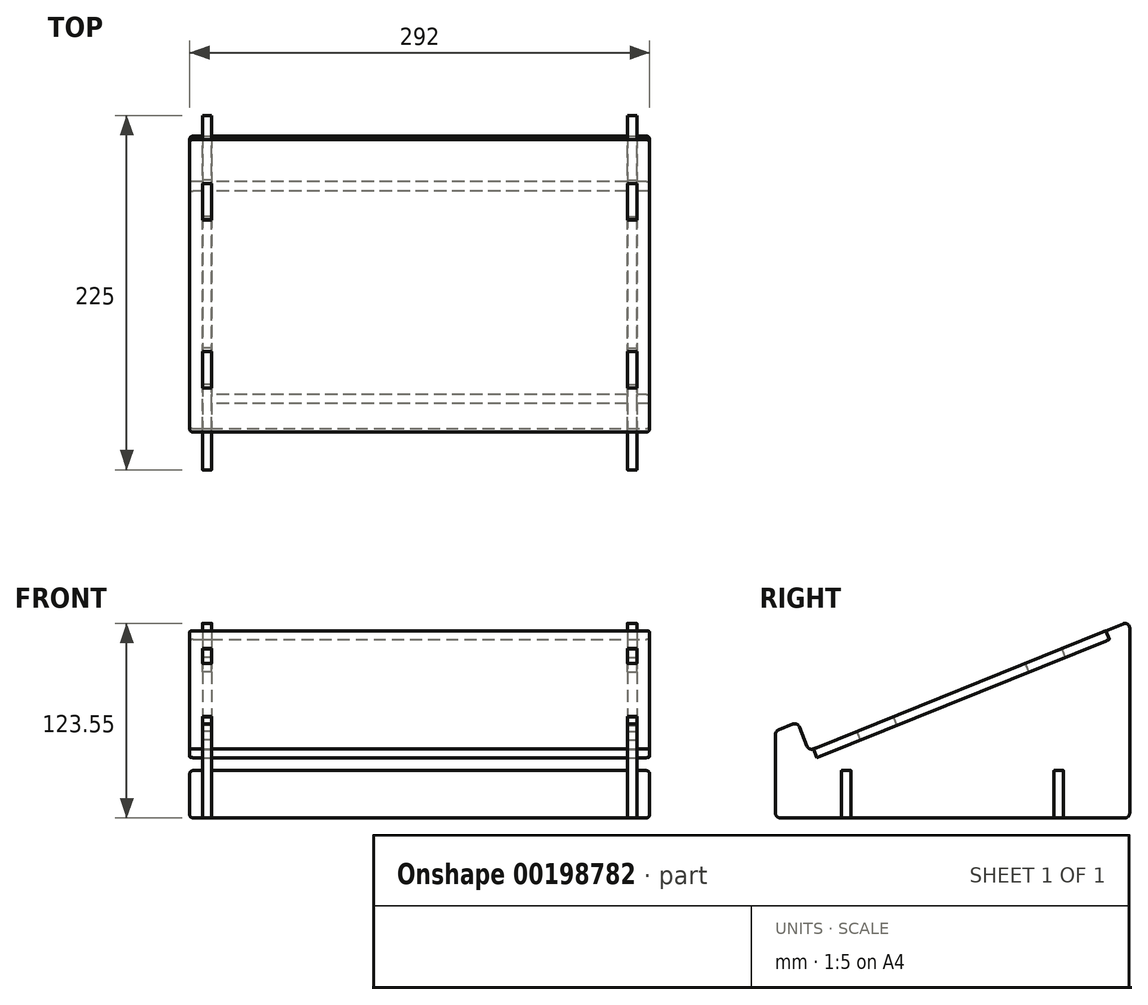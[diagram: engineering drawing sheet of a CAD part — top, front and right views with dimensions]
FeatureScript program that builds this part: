
annotation { "Feature Type Name" : "Feature", "Feature Type Description" : "" }
export const myFeature = defineFeature(function(context is Context, id is Id, definition is map)
    precondition{}
    {
        {
            var Q0;
            Q0=qCreatedBy(makeId("Right.planeOp"),FACE);
            var sketch = newSketch(context, id + "F0", { "sketchPlane" : qUnion([Q0])});
            skLineSegment(sketch, "E0", {"start": v(0, 0) * mm, "end": v(225, 0) * mm});
            skLineSegment(sketch, "E1", {"start": v(225, 0) * mm, "end": v(225, 125) * mm});
            skLineSegment(sketch, "E2", {"start": v(225, 125) * mm, "end": v(21.26, 42.68) * mm});
            skLineSegment(sketch, "E3", {"start": v(21.26, 42.68) * mm, "end": v(14, 60.66) * mm});
            skLineSegment(sketch, "E4", {"start": v(14, 60.66) * mm, "end": v(0, 55) * mm});
            skLineSegment(sketch, "E5", {"start": v(0, 55) * mm, "end": v(0, 0) * mm});
            skSolve(sketch);
        }
        {
            var Q0;
            Q0=makeQuery(id+"F0.imprint","IMPRINT",FACE,{"disambiguationData":[TD([[makeQuery(id+"F0.imprint","IMPRINT",EDGE,{"derivedFrom":sQuery(id+"F0.wireOp",EDGE,"E0")}),1.0]])]});
            extrude(context, id + "F1", {"entities" : qUnion([Q0]), "depth" : 6 * mm});
        }
        {
            var Q0;
            Q0=makeQuery(id+"F1.opExtrude","SWEPT_EDGE",EDGE,{"disambiguationData":[OSD([sQuery(id+"F0.wireOp",EDGE,"E1"),sQuery(id+"F0.wireOp",EDGE,"E2")])]});
            var Q1;
            Q1=makeQuery(id+"F1.opExtrude","SWEPT_EDGE",EDGE,{"disambiguationData":[OSD([sQuery(id+"F0.wireOp",EDGE,"E0"),sQuery(id+"F0.wireOp",EDGE,"E1")])]});
            var Q2;
            Q2=makeQuery(id+"F1.opExtrude","SWEPT_EDGE",EDGE,{"disambiguationData":[OSD([sQuery(id+"F0.wireOp",EDGE,"E4"),sQuery(id+"F0.wireOp",EDGE,"E5")])]});
            var Q3;
            Q3=makeQuery(id+"F1.opExtrude","SWEPT_EDGE",EDGE,{"disambiguationData":[OSD([sQuery(id+"F0.wireOp",EDGE,"E3"),sQuery(id+"F0.wireOp",EDGE,"E4")])]});
            var Q4;
            Q4=makeQuery(id+"F1.opExtrude","SWEPT_EDGE",EDGE,{"disambiguationData":[OSD([sQuery(id+"F0.wireOp",EDGE,"E2"),sQuery(id+"F0.wireOp",EDGE,"E3")])]});
            var Q5;
            Q5=makeQuery(id+"F1.opExtrude","SWEPT_EDGE",EDGE,{"disambiguationData":[OSD([sQuery(id+"F0.wireOp",EDGE,"E0"),sQuery(id+"F0.wireOp",EDGE,"E5")])]});
            fillet(context, id + "F2", {"entities" : qUnion([Q0, Q1, Q2, Q3, Q4, Q5]), "radius" : 3 * mm, "tangentPropagation" : true, "allowEdgeOverflow" : false});
        }
        {
            var Q0;
            Q0=makeQuery(id+"F1.opExtrude","SWEPT_BODY",BODY,{"disambiguationData":[OSD([sQuery(id+"F0.wireOp",EDGE,"E0"),sQuery(id+"F0.wireOp",EDGE,"E1"),sQuery(id+"F0.wireOp",EDGE,"E2"),sQuery(id+"F0.wireOp",EDGE,"E3"),sQuery(id+"F0.wireOp",EDGE,"E4"),sQuery(id+"F0.wireOp",EDGE,"E5")])]});
            transform(context, id + "F3", {"entities" : qUnion([Q0]), "transformType" : TransformType.TRANSLATION_3D, "dx" : 270 * mm, "dy" : 0 * mm, "dz" : 0 * mm, "makeCopy" : true});
        }
        {
            var Q0;
            Q0=makeQuery(id+"F1.opExtrude","SWEPT_FACE",FACE,{"disambiguationData":[OSD([sQuery(id+"F0.wireOp",EDGE,"E2")])]});
            var sketch = newSketch(context, id + "F4", { "sketchPlane" : qUnion([Q0])});
            skLineSegment(sketch, "E6.bottom", {"start": v(-8, 239) * mm, "end": v(284, 239) * mm});
            skLineSegment(sketch, "E6.top", {"start": v(-8, 38.7) * mm, "end": v(284, 38.7) * mm});
            skLineSegment(sketch, "E6.left", {"start": v(-8, 239) * mm, "end": v(-8, 38.7) * mm});
            skLineSegment(sketch, "E6.right", {"start": v(284, 239) * mm, "end": v(284, 38.7) * mm});
            skLineSegment(sketch, "E7.bottom", {"start": v(270, 209) * mm, "end": v(276, 209) * mm});
            skLineSegment(sketch, "E7.top", {"start": v(270, 184) * mm, "end": v(276, 184) * mm});
            skLineSegment(sketch, "E7.left", {"start": v(270, 209) * mm, "end": v(270, 184) * mm});
            skLineSegment(sketch, "E7.right", {"start": v(276, 209) * mm, "end": v(276, 184) * mm});
            skLineSegment(sketch, "E8", {"start": v(138, 239) * mm, "end": v(138, 38.7) * mm, "construction": true});
            skLineSegment(sketch, "E9", {"start": v(-8, 138.85) * mm, "end": v(284, 138.85) * mm, "construction": true});
            skLineSegment(sketch, "E10.MirrorCS", {"start": v(6, 209) * mm, "end": v(6, 184) * mm});
            skLineSegment(sketch, "E11.MirrorCS", {"start": v(6, 209) * mm, "end": v(0, 209) * mm});
            skLineSegment(sketch, "E12.MirrorCS", {"start": v(0, 209) * mm, "end": v(0, 184) * mm});
            skLineSegment(sketch, "E13.MirrorCS", {"start": v(6, 184) * mm, "end": v(0, 184) * mm});
            skLineSegment(sketch, "E14.MirrorCS", {"start": v(6, 68.7) * mm, "end": v(6, 93.7) * mm});
            skLineSegment(sketch, "E15.MirrorCS", {"start": v(6, 68.7) * mm, "end": v(0, 68.7) * mm});
            skLineSegment(sketch, "E16.MirrorCS", {"start": v(0, 68.7) * mm, "end": v(0, 93.7) * mm});
            skLineSegment(sketch, "E17.MirrorCS", {"start": v(6, 93.7) * mm, "end": v(0, 93.7) * mm});
            skLineSegment(sketch, "E18.MirrorCS", {"start": v(270, 68.7) * mm, "end": v(276, 68.7) * mm});
            skLineSegment(sketch, "E19.MirrorCS", {"start": v(270, 93.7) * mm, "end": v(276, 93.7) * mm});
            skLineSegment(sketch, "E20.MirrorCS", {"start": v(276, 68.7) * mm, "end": v(276, 93.7) * mm});
            skLineSegment(sketch, "E21.MirrorCS", {"start": v(270, 68.7) * mm, "end": v(270, 93.7) * mm});
            skSolve(sketch);
        }
        {
            var Q0;
            {var subQ1=sQuery(id+"F4.wireOp",EDGE,"E6.right");Q0=makeQuery(id+"F4.imprint","IMPRINT",FACE,{"disambiguationData":[TD([[makeQuery(id+"F4.imprint","IMPRINT",EDGE,{"derivedFrom":subQ1}),-1.0]])]});}
            var Q1;
            {var subQ0=sQuery(id+"F4.wireOp",EDGE,"E13.MirrorCS");Q1=makeQuery(id+"F4.imprint","IMPRINT",FACE,{"disambiguationData":[TD([[makeQuery(id+"F4.imprint","IMPRINT",EDGE,{"derivedFrom":subQ0}),1.0]])]});}
            var Q2;
            {var subQ1=sQuery(id+"F4.wireOp",EDGE,"E6.left");Q2=makeQuery(id+"F4.imprint","IMPRINT",FACE,{"disambiguationData":[TD([[makeQuery(id+"F4.imprint","IMPRINT",EDGE,{"derivedFrom":subQ1}),1.0]])]});}
            var Q3;
            {var subQ6=sQuery(id+"F4.wireOp",EDGE,"E11.MirrorCS");Q3=makeQuery(id+"F4.imprint","IMPRINT",FACE,{"disambiguationData":[TD([[makeQuery(id+"F4.imprint","IMPRINT",EDGE,{"derivedFrom":subQ6}),-1.0]])]});}
            var Q4;
            {var subQ6=sQuery(id+"F4.wireOp",EDGE,"E15.MirrorCS");Q4=makeQuery(id+"F4.imprint","IMPRINT",FACE,{"disambiguationData":[TD([[makeQuery(id+"F4.imprint","IMPRINT",EDGE,{"derivedFrom":subQ6}),1.0]])]});}
            extrude(context, id + "F5", {"entities" : qUnion([Q0, Q1, Q2, Q3, Q4]), "oppositeDirection" : true, "depth" : 6 * mm});
        }
        {
            var Q0;
            Q0=makeQuery(id+"F5.opExtrude","SWEPT_BODY",BODY,{"disambiguationData":[OSD([sQuery(id+"F4.wireOp",EDGE,"E6.bottom"),sQuery(id+"F4.wireOp",EDGE,"E6.top"),sQuery(id+"F4.wireOp",EDGE,"E6.left"),sQuery(id+"F4.wireOp",EDGE,"E6.right"),sQuery(id+"F4.wireOp",EDGE,"E7.bottom"),sQuery(id+"F4.wireOp",EDGE,"E7.top"),sQuery(id+"F4.wireOp",EDGE,"E7.left"),sQuery(id+"F4.wireOp",EDGE,"E7.right"),sQuery(id+"F4.wireOp",EDGE,"E10.MirrorCS"),sQuery(id+"F4.wireOp",EDGE,"E11.MirrorCS"),sQuery(id+"F4.wireOp",EDGE,"E12.MirrorCS"),sQuery(id+"F4.wireOp",EDGE,"E13.MirrorCS"),sQuery(id+"F4.wireOp",EDGE,"E14.MirrorCS"),sQuery(id+"F4.wireOp",EDGE,"E15.MirrorCS"),sQuery(id+"F4.wireOp",EDGE,"E16.MirrorCS"),sQuery(id+"F4.wireOp",EDGE,"E17.MirrorCS"),sQuery(id+"F4.wireOp",EDGE,"E18.MirrorCS"),sQuery(id+"F4.wireOp",EDGE,"E19.MirrorCS"),sQuery(id+"F4.wireOp",EDGE,"E20.MirrorCS"),sQuery(id+"F4.wireOp",EDGE,"E21.MirrorCS")])]});
            var Q1;
            Q1=makeQuery(id+"F1.opExtrude","SWEPT_BODY",BODY,{"disambiguationData":[OSD([sQuery(id+"F0.wireOp",EDGE,"E0"),sQuery(id+"F0.wireOp",EDGE,"E1"),sQuery(id+"F0.wireOp",EDGE,"E2"),sQuery(id+"F0.wireOp",EDGE,"E3"),sQuery(id+"F0.wireOp",EDGE,"E4"),sQuery(id+"F0.wireOp",EDGE,"E5")])]});
            var Q2;
            Q2=makeQuery(id+"F3.opPattern","COPY",BODY,{"derivedFrom":makeQuery(id+"F1.opExtrude","SWEPT_BODY",BODY,{"disambiguationData":[OSD([sQuery(id+"F0.wireOp",EDGE,"E0"),sQuery(id+"F0.wireOp",EDGE,"E1"),sQuery(id+"F0.wireOp",EDGE,"E2"),sQuery(id+"F0.wireOp",EDGE,"E3"),sQuery(id+"F0.wireOp",EDGE,"E4"),sQuery(id+"F0.wireOp",EDGE,"E5")])]}),"instanceName":"1"});
            booleanBodies(context, id + "F6", {"operationType" : BooleanOperationType.SUBTRACTION, "tools" : qUnion([Q0]), "targets" : qUnion([Q1, Q2]), "keepTools" : true});
        }
        {
            var Q0;
            Q0=makeQuery(id+"F5.opExtrude","SWEPT_EDGE",EDGE,{"disambiguationData":[OSD([sQuery(id+"F4.wireOp",EDGE,"E6.top"),sQuery(id+"F4.wireOp",EDGE,"E6.right")])]});
            var Q1;
            Q1=makeQuery(id+"F5.opExtrude","SWEPT_EDGE",EDGE,{"disambiguationData":[OSD([sQuery(id+"F4.wireOp",EDGE,"E6.bottom"),sQuery(id+"F4.wireOp",EDGE,"E6.right")])]});
            var Q2;
            Q2=makeQuery(id+"F5.opExtrude","SWEPT_EDGE",EDGE,{"disambiguationData":[OSD([sQuery(id+"F4.wireOp",EDGE,"E6.top"),sQuery(id+"F4.wireOp",EDGE,"E6.left")])]});
            var Q3;
            Q3=makeQuery(id+"F5.opExtrude","SWEPT_EDGE",EDGE,{"disambiguationData":[OSD([sQuery(id+"F4.wireOp",EDGE,"E6.bottom"),sQuery(id+"F4.wireOp",EDGE,"E6.left")])]});
            fillet(context, id + "F7", {"entities" : qUnion([Q0, Q1, Q2, Q3]), "radius" : 2 * mm, "tangentPropagation" : true, "allowEdgeOverflow" : false});
        }
        {
            var Q0;
            Q0=makeQuery(id+"F3.opPattern","COPY",FACE,{"derivedFrom":makeQuery(id+"F1.opExtrude","SWEPT_FACE",FACE,{"disambiguationData":[OSD([sQuery(id+"F0.wireOp",EDGE,"E1")])]}),"instanceName":"1"});
            cPlane(context, id + "F8", {"entities" : qUnion([Q0]), "cplaneType" : CPlaneType.OFFSET, "offset" : 45 * mm, "oppositeDirection" : true, "width" : 150 * mm, "height" : 150 * mm});
        }
        {
            var Q0;
            Q0=qCreatedBy(id+"F8.planeOp",FACE);
            var sketch = newSketch(context, id + "F9", { "sketchPlane" : qUnion([Q0])});
            skLineSegment(sketch, "E22.bottom", {"start": v(-284, 0) * mm, "end": v(8, 0) * mm});
            skLineSegment(sketch, "E22.top", {"start": v(-284, 30) * mm, "end": v(8, 30) * mm});
            skLineSegment(sketch, "E22.left", {"start": v(-284, 0) * mm, "end": v(-284, 30) * mm});
            skLineSegment(sketch, "E22.right", {"start": v(8, 0) * mm, "end": v(8, 30) * mm});
            skLineSegment(sketch, "E23", {"start": v(-284, 15) * mm, "end": v(8, 15) * mm});
            skLineSegment(sketch, "E24.bottom", {"start": v(-276, 0) * mm, "end": v(-270, 0) * mm});
            skLineSegment(sketch, "E24.top", {"start": v(-276, 30) * mm, "end": v(-270, 30) * mm});
            skLineSegment(sketch, "E24.left", {"start": v(-276, 0) * mm, "end": v(-276, 30) * mm});
            skLineSegment(sketch, "E24.right", {"start": v(-270, 0) * mm, "end": v(-270, 30) * mm});
            skLineSegment(sketch, "E25.bottom", {"start": v(0, 0) * mm, "end": v(-6, 0) * mm});
            skLineSegment(sketch, "E25.top", {"start": v(0, 30) * mm, "end": v(-6, 30) * mm});
            skLineSegment(sketch, "E25.left", {"start": v(0, 0) * mm, "end": v(0, 30) * mm});
            skLineSegment(sketch, "E25.right", {"start": v(-6, 0) * mm, "end": v(-6, 30) * mm});
            skSolve(sketch);
        }
        {
            var Q0;
            {var subQ0=sQuery(id+"F9.wireOp",EDGE,"E24.right");var subQ5=sQuery(id+"F9.wireOp",EDGE,"E23");var subQ6=makeQuery(id+"F9.imprint","INTERSECT",VERTEX,{"derivedFrom":[subQ5,subQ0]});Q0=makeQuery(id+"F9.imprint","IMPRINT",FACE,{"disambiguationData":[TD([[makeQuery(id+"F9.imprint","IMPRINT",EDGE,{"disambiguationData":[TD([[subQ6,-1.0]])],"derivedFrom":subQ5}),1.0]])]});}
            var Q1;
            {var subQ0=sQuery(id+"F9.wireOp",EDGE,"E24.right");var subQ5=sQuery(id+"F9.wireOp",EDGE,"E23");var subQ6=makeQuery(id+"F9.imprint","INTERSECT",VERTEX,{"derivedFrom":[subQ5,subQ0]});Q1=makeQuery(id+"F9.imprint","IMPRINT",FACE,{"disambiguationData":[TD([[makeQuery(id+"F9.imprint","IMPRINT",EDGE,{"disambiguationData":[TD([[subQ6,-1.0]])],"derivedFrom":subQ5}),-1.0]])]});}
            var Q2;
            {var subQ0=sQuery(id+"F9.wireOp",EDGE,"E22.right");var subQ1=sQuery(id+"F9.wireOp",EDGE,"E22.top");var subQ2=makeQuery(id+"F9.imprint","INTERSECT",VERTEX,{"derivedFrom":[subQ1,subQ0]});Q2=makeQuery(id+"F9.imprint","IMPRINT",FACE,{"disambiguationData":[TD([[makeQuery(id+"F9.imprint","IMPRINT",EDGE,{"disambiguationData":[TD([[subQ2,1.0]])],"derivedFrom":subQ0}),1.0]])]});}
            var Q3;
            {var subQ0=sQuery(id+"F9.wireOp",EDGE,"E22.right");var subQ1=sQuery(id+"F9.wireOp",EDGE,"E22.bottom");var subQ2=makeQuery(id+"F9.imprint","INTERSECT",VERTEX,{"derivedFrom":[subQ1,subQ0]});Q3=makeQuery(id+"F9.imprint","IMPRINT",FACE,{"disambiguationData":[TD([[makeQuery(id+"F9.imprint","IMPRINT",EDGE,{"disambiguationData":[TD([[subQ2,-1.0]])],"derivedFrom":subQ0}),1.0]])]});}
            var Q4;
            {var subQ0=sQuery(id+"F9.wireOp",EDGE,"E22.left");var subQ1=sQuery(id+"F9.wireOp",EDGE,"E22.bottom");var subQ2=makeQuery(id+"F9.imprint","INTERSECT",VERTEX,{"derivedFrom":[subQ1,subQ0]});Q4=makeQuery(id+"F9.imprint","IMPRINT",FACE,{"disambiguationData":[TD([[makeQuery(id+"F9.imprint","IMPRINT",EDGE,{"disambiguationData":[TD([[subQ2,-1.0]])],"derivedFrom":subQ0}),-1.0]])]});}
            var Q5;
            {var subQ0=sQuery(id+"F9.wireOp",EDGE,"E22.left");var subQ1=sQuery(id+"F9.wireOp",EDGE,"E22.top");var subQ2=makeQuery(id+"F9.imprint","INTERSECT",VERTEX,{"derivedFrom":[subQ1,subQ0]});Q5=makeQuery(id+"F9.imprint","IMPRINT",FACE,{"disambiguationData":[TD([[makeQuery(id+"F9.imprint","IMPRINT",EDGE,{"disambiguationData":[TD([[subQ2,1.0]])],"derivedFrom":subQ0}),-1.0]])]});}
            var Q6;
            {var subQ5=sQuery(id+"F9.wireOp",EDGE,"E24.bottom");Q6=makeQuery(id+"F9.imprint","IMPRINT",FACE,{"disambiguationData":[TD([[makeQuery(id+"F9.imprint","IMPRINT",EDGE,{"derivedFrom":subQ5}),1.0]])]});}
            var Q7;
            {var subQ5=sQuery(id+"F9.wireOp",EDGE,"E25.bottom");Q7=makeQuery(id+"F9.imprint","IMPRINT",FACE,{"disambiguationData":[TD([[makeQuery(id+"F9.imprint","IMPRINT",EDGE,{"derivedFrom":subQ5}),-1.0]])]});}
            extrude(context, id + "F10", {"entities" : qUnion([Q0, Q1, Q2, Q3, Q4, Q5, Q6, Q7]), "endBound" : BoundingType.SYMMETRIC, "depth" : 6 * mm});
        }
        {
            var Q0;
            Q0=makeQuery(id+"F10.opExtrude","SWEPT_EDGE",EDGE,{"disambiguationData":[OSD([sQuery(id+"F9.wireOp",EDGE,"E22.top"),sQuery(id+"F9.wireOp",EDGE,"E22.left")])]});
            var Q1;
            Q1=makeQuery(id+"F10.opExtrude","SWEPT_EDGE",EDGE,{"disambiguationData":[OSD([sQuery(id+"F9.wireOp",EDGE,"E22.bottom"),sQuery(id+"F9.wireOp",EDGE,"E22.left")])]});
            var Q2;
            Q2=makeQuery(id+"F10.opExtrude","SWEPT_EDGE",EDGE,{"disambiguationData":[OSD([sQuery(id+"F9.wireOp",EDGE,"E22.top"),sQuery(id+"F9.wireOp",EDGE,"E22.right")])]});
            var Q3;
            Q3=makeQuery(id+"F10.opExtrude","SWEPT_EDGE",EDGE,{"disambiguationData":[OSD([sQuery(id+"F9.wireOp",EDGE,"E22.bottom"),sQuery(id+"F9.wireOp",EDGE,"E22.right")])]});
            fillet(context, id + "F11", {"entities" : qUnion([Q0, Q1, Q2, Q3]), "radius" : 2 * mm, "tangentPropagation" : true, "allowEdgeOverflow" : false});
        }
        {
            var Q0;
            Q0=makeQuery(id+"F10.opExtrude","SWEPT_EDGE",EDGE,{"disambiguationData":[OSD([sQuery(id+"F9.wireOp",EDGE,"E22.top"),sQuery(id+"F9.wireOp",EDGE,"E24.top"),sQuery(id+"F9.wireOp",EDGE,"E24.right")])]});
            var Q1;
            Q1=makeQuery(id+"F10.opExtrude","SWEPT_EDGE",EDGE,{"disambiguationData":[OSD([sQuery(id+"F9.wireOp",EDGE,"E22.top"),sQuery(id+"F9.wireOp",EDGE,"E24.top"),sQuery(id+"F9.wireOp",EDGE,"E24.left")])]});
            var Q2;
            Q2=makeQuery(id+"F10.opExtrude","SWEPT_EDGE",EDGE,{"disambiguationData":[OSD([sQuery(id+"F9.wireOp",EDGE,"E22.top"),sQuery(id+"F9.wireOp",EDGE,"E25.top"),sQuery(id+"F9.wireOp",EDGE,"E25.left")])]});
            var Q3;
            Q3=makeQuery(id+"F10.opExtrude","SWEPT_EDGE",EDGE,{"disambiguationData":[OSD([sQuery(id+"F9.wireOp",EDGE,"E22.top"),sQuery(id+"F9.wireOp",EDGE,"E25.top"),sQuery(id+"F9.wireOp",EDGE,"E25.right")])]});
            fillet(context, id + "F12", {"entities" : qUnion([Q0, Q1, Q2, Q3]), "radius" : .5 * mm, "tangentPropagation" : true, "allowEdgeOverflow" : false});
        }
        {
            var Q0;
            Q0=makeQuery(id+"F3.opPattern","COPY",FACE,{"derivedFrom":makeQuery(id+"F1.opExtrude","SWEPT_FACE",FACE,{"disambiguationData":[OSD([sQuery(id+"F0.wireOp",EDGE,"E1")])]}),"instanceName":"1"});
            var Q1;
            Q1=makeQuery(id+"F3.opPattern","COPY",FACE,{"derivedFrom":makeQuery(id+"F1.opExtrude","SWEPT_FACE",FACE,{"disambiguationData":[OSD([sQuery(id+"F0.wireOp",EDGE,"E5")])]}),"instanceName":"1"});
            cPlane(context, id + "F13", {"entities" : qUnion([Q0, Q1]), "cplaneType" : CPlaneType.MID_PLANE, "offset" : 25 * mm, "width" : 150 * mm, "height" : 150 * mm});
        }
        {
            var Q0;
            Q0=makeQuery(id+"F10.opExtrude","SWEPT_BODY",BODY,{"disambiguationData":[OSD([sQuery(id+"F9.wireOp",EDGE,"E22.bottom"),sQuery(id+"F9.wireOp",EDGE,"E22.top"),sQuery(id+"F9.wireOp",EDGE,"E22.left"),sQuery(id+"F9.wireOp",EDGE,"E23"),sQuery(id+"F9.wireOp",EDGE,"E24.bottom"),sQuery(id+"F9.wireOp",EDGE,"E24.left"),sQuery(id+"F9.wireOp",EDGE,"E24.right"),sQuery(id+"F9.wireOp",EDGE,"E25.right")])]});
            var Q1;
            Q1=qCreatedBy(id+"F13.planeOp",FACE);
            mirror(context, id + "F14", {"entities" : qUnion([Q0]), "mirrorPlane" : qUnion([Q1])});
        }
        {
            var Q0;
            Q0=makeQuery(id+"F10.opExtrude","SWEPT_BODY",BODY,{"disambiguationData":[OSD([sQuery(id+"F9.wireOp",EDGE,"E22.bottom"),sQuery(id+"F9.wireOp",EDGE,"E22.top"),sQuery(id+"F9.wireOp",EDGE,"E22.left"),sQuery(id+"F9.wireOp",EDGE,"E22.right"),sQuery(id+"F9.wireOp",EDGE,"E23"),sQuery(id+"F9.wireOp",EDGE,"E24.bottom"),sQuery(id+"F9.wireOp",EDGE,"E24.left"),sQuery(id+"F9.wireOp",EDGE,"E24.right"),sQuery(id+"F9.wireOp",EDGE,"E25.bottom"),sQuery(id+"F9.wireOp",EDGE,"E25.left"),sQuery(id+"F9.wireOp",EDGE,"E25.right")])]});
            var Q1;
            Q1=makeQuery(id+"F14.opPattern","COPY",BODY,{"derivedFrom":makeQuery(id+"F10.opExtrude","SWEPT_BODY",BODY,{"disambiguationData":[OSD([sQuery(id+"F9.wireOp",EDGE,"E22.bottom"),sQuery(id+"F9.wireOp",EDGE,"E22.top"),sQuery(id+"F9.wireOp",EDGE,"E22.left"),sQuery(id+"F9.wireOp",EDGE,"E22.right"),sQuery(id+"F9.wireOp",EDGE,"E23"),sQuery(id+"F9.wireOp",EDGE,"E24.bottom"),sQuery(id+"F9.wireOp",EDGE,"E24.left"),sQuery(id+"F9.wireOp",EDGE,"E24.right"),sQuery(id+"F9.wireOp",EDGE,"E25.bottom"),sQuery(id+"F9.wireOp",EDGE,"E25.left"),sQuery(id+"F9.wireOp",EDGE,"E25.right")])]}),"instanceName":"1"});
            var Q2;
            Q2=makeQuery(id+"F1.opExtrude","SWEPT_BODY",BODY,{"disambiguationData":[OSD([sQuery(id+"F0.wireOp",EDGE,"E0"),sQuery(id+"F0.wireOp",EDGE,"E1"),sQuery(id+"F0.wireOp",EDGE,"E2"),sQuery(id+"F0.wireOp",EDGE,"E3"),sQuery(id+"F0.wireOp",EDGE,"E4"),sQuery(id+"F0.wireOp",EDGE,"E5")])]});
            var Q3;
            Q3=makeQuery(id+"F3.opPattern","COPY",BODY,{"derivedFrom":makeQuery(id+"F1.opExtrude","SWEPT_BODY",BODY,{"disambiguationData":[OSD([sQuery(id+"F0.wireOp",EDGE,"E0"),sQuery(id+"F0.wireOp",EDGE,"E1"),sQuery(id+"F0.wireOp",EDGE,"E2"),sQuery(id+"F0.wireOp",EDGE,"E3"),sQuery(id+"F0.wireOp",EDGE,"E4"),sQuery(id+"F0.wireOp",EDGE,"E5")])]}),"instanceName":"1"});
            booleanBodies(context, id + "F15", {"operationType" : BooleanOperationType.SUBTRACTION, "tools" : qUnion([Q0, Q1]), "targets" : qUnion([Q2, Q3]), "keepTools" : true});
        }
        {
            var Q0;
            {var subQ0=sQuery(id+"F0.wireOp",EDGE,"E2");Q0=makeQuery(id+"F6.opBoolean","MERGE",EDGE,{"derivedFrom":[makeQuery(id+"F3.opPattern","COPY",EDGE,{"derivedFrom":makeQuery(id+"F2.opFillet","BLEND_EDGE",EDGE,{"blendedFrom":[makeQuery(id+"F1.opExtrude","SWEPT_EDGE",EDGE,{"disambiguationData":[OSD([subQ0,sQuery(id+"F0.wireOp",EDGE,"E3")])]}),makeQuery(id+"F1.opExtrude","SWEPT_FACE",FACE,{"disambiguationData":[OSD([subQ0])]})],"blendedInto":[makeQuery(id+"F1.opExtrude","SWEPT_FACE",FACE,{"disambiguationData":[OSD([subQ0])]})]}),"instanceName":"1"}),makeQuery(id+"F5.opExtrude","CAP_EDGE",EDGE,{"disambiguationData":[OSD([sQuery(id+"F4.wireOp",EDGE,"E6.top")])],"isStart":true})]});}
            var Q1;
            Q1=makeQuery(id+"F6.opBoolean","COPY",EDGE,{"derivedFrom":makeQuery(id+"F5.opExtrude","CAP_EDGE",EDGE,{"disambiguationData":[OSD([sQuery(id+"F4.wireOp",EDGE,"E18.MirrorCS")])],"isStart":true})});
            var Q2;
            Q2=makeQuery(id+"F6.opBoolean","COPY",EDGE,{"derivedFrom":makeQuery(id+"F5.opExtrude","CAP_EDGE",EDGE,{"disambiguationData":[OSD([sQuery(id+"F4.wireOp",EDGE,"E19.MirrorCS")])],"isStart":true})});
            var Q3;
            Q3=makeQuery(id+"F6.opBoolean","COPY",EDGE,{"derivedFrom":makeQuery(id+"F5.opExtrude","CAP_EDGE",EDGE,{"disambiguationData":[OSD([sQuery(id+"F4.wireOp",EDGE,"E7.top")])],"isStart":true})});
            var Q4;
            Q4=makeQuery(id+"F6.opBoolean","COPY",EDGE,{"derivedFrom":makeQuery(id+"F5.opExtrude","CAP_EDGE",EDGE,{"disambiguationData":[OSD([sQuery(id+"F4.wireOp",EDGE,"E7.bottom")])],"isStart":true})});
            var Q5;
            {var subQ3=sQuery(id+"F0.wireOp",EDGE,"E2");var subQ6=sQuery(id+"F4.wireOp",EDGE,"E6.bottom");Q5=makeQuery(id+"F6.opBoolean","COPY",EDGE,{"disambiguationData":[TD([makeQuery(id+"F3.opPattern","COPY",FACE,{"derivedFrom":makeQuery(id+"F1.opExtrude","SWEPT_FACE",FACE,{"disambiguationData":[OSD([subQ3])]}),"instanceName":"1"})])],"derivedFrom":makeQuery(id+"F5.opExtrude","CAP_EDGE",EDGE,{"disambiguationData":[OSD([subQ6])],"isStart":true})});}
            var Q6;
            {var subQ0=sQuery(id+"F0.wireOp",EDGE,"E2");Q6=makeQuery(id+"F6.opBoolean","MERGE",EDGE,{"derivedFrom":[makeQuery(id+"F2.opFillet","BLEND_EDGE",EDGE,{"blendedFrom":[makeQuery(id+"F1.opExtrude","SWEPT_EDGE",EDGE,{"disambiguationData":[OSD([subQ0,sQuery(id+"F0.wireOp",EDGE,"E3")])]}),makeQuery(id+"F1.opExtrude","SWEPT_FACE",FACE,{"disambiguationData":[OSD([subQ0])]})],"blendedInto":[makeQuery(id+"F1.opExtrude","SWEPT_FACE",FACE,{"disambiguationData":[OSD([subQ0])]})]}),makeQuery(id+"F5.opExtrude","CAP_EDGE",EDGE,{"disambiguationData":[OSD([sQuery(id+"F4.wireOp",EDGE,"E6.top")])],"isStart":true})]});}
            var Q7;
            Q7=makeQuery(id+"F6.opBoolean","COPY",EDGE,{"derivedFrom":makeQuery(id+"F5.opExtrude","CAP_EDGE",EDGE,{"disambiguationData":[OSD([sQuery(id+"F4.wireOp",EDGE,"E15.MirrorCS")])],"isStart":true})});
            var Q8;
            Q8=makeQuery(id+"F6.opBoolean","COPY",EDGE,{"derivedFrom":makeQuery(id+"F5.opExtrude","CAP_EDGE",EDGE,{"disambiguationData":[OSD([sQuery(id+"F4.wireOp",EDGE,"E17.MirrorCS")])],"isStart":true})});
            var Q9;
            Q9=makeQuery(id+"F6.opBoolean","COPY",EDGE,{"derivedFrom":makeQuery(id+"F5.opExtrude","CAP_EDGE",EDGE,{"disambiguationData":[OSD([sQuery(id+"F4.wireOp",EDGE,"E13.MirrorCS")])],"isStart":true})});
            var Q10;
            Q10=makeQuery(id+"F6.opBoolean","COPY",EDGE,{"derivedFrom":makeQuery(id+"F5.opExtrude","CAP_EDGE",EDGE,{"disambiguationData":[OSD([sQuery(id+"F4.wireOp",EDGE,"E11.MirrorCS")])],"isStart":true})});
            var Q11;
            {var subQ3=sQuery(id+"F0.wireOp",EDGE,"E2");var subQ6=sQuery(id+"F4.wireOp",EDGE,"E6.bottom");Q11=makeQuery(id+"F6.opBoolean","COPY",EDGE,{"disambiguationData":[TD([makeQuery(id+"F1.opExtrude","SWEPT_FACE",FACE,{"disambiguationData":[OSD([subQ3])]})])],"derivedFrom":makeQuery(id+"F5.opExtrude","CAP_EDGE",EDGE,{"disambiguationData":[OSD([subQ6])],"isStart":true})});}
            var Q12;
            {var subQ0=sQuery(id+"F0.wireOp",EDGE,"E0");var subQ6=sQuery(id+"F9.wireOp",EDGE,"E25.bottom");var subQ7=sQuery(id+"F9.wireOp",EDGE,"E24.bottom");var subQ8=sQuery(id+"F9.wireOp",EDGE,"E22.bottom");Q12=makeQuery(id+"F15.opBoolean","COPY",EDGE,{"disambiguationData":[TD([makeQuery(id+"F1.opExtrude","SWEPT_FACE",FACE,{"disambiguationData":[OSD([subQ0])]})])],"derivedFrom":makeQuery(id+"F10.opExtrude","CAP_EDGE",EDGE,{"disambiguationData":[OSD([subQ8,subQ7,subQ6])],"isStart":false})});}
            var Q13;
            {var subQ0=sQuery(id+"F0.wireOp",EDGE,"E0");var subQ6=sQuery(id+"F9.wireOp",EDGE,"E25.bottom");var subQ7=sQuery(id+"F9.wireOp",EDGE,"E24.bottom");var subQ8=sQuery(id+"F9.wireOp",EDGE,"E22.bottom");Q13=makeQuery(id+"F15.opBoolean","COPY",EDGE,{"disambiguationData":[TD([makeQuery(id+"F1.opExtrude","SWEPT_FACE",FACE,{"disambiguationData":[OSD([subQ0])]})])],"derivedFrom":makeQuery(id+"F10.opExtrude","CAP_EDGE",EDGE,{"disambiguationData":[OSD([subQ8,subQ7,subQ6])],"isStart":true})});}
            var Q14;
            {var subQ0=sQuery(id+"F0.wireOp",EDGE,"E0");var subQ6=sQuery(id+"F9.wireOp",EDGE,"E25.bottom");var subQ7=sQuery(id+"F9.wireOp",EDGE,"E24.bottom");var subQ8=sQuery(id+"F9.wireOp",EDGE,"E22.bottom");Q14=makeQuery(id+"F15.opBoolean","COPY",EDGE,{"disambiguationData":[TD([makeQuery(id+"F1.opExtrude","SWEPT_FACE",FACE,{"disambiguationData":[OSD([subQ0])]})])],"derivedFrom":makeQuery(id+"F14.opPattern","COPY",EDGE,{"derivedFrom":makeQuery(id+"F10.opExtrude","CAP_EDGE",EDGE,{"disambiguationData":[OSD([subQ8,subQ7,subQ6])],"isStart":true}),"instanceName":"1"})});}
            var Q15;
            {var subQ0=sQuery(id+"F0.wireOp",EDGE,"E0");var subQ6=sQuery(id+"F9.wireOp",EDGE,"E25.bottom");var subQ7=sQuery(id+"F9.wireOp",EDGE,"E24.bottom");var subQ8=sQuery(id+"F9.wireOp",EDGE,"E22.bottom");Q15=makeQuery(id+"F15.opBoolean","COPY",EDGE,{"disambiguationData":[TD([makeQuery(id+"F1.opExtrude","SWEPT_FACE",FACE,{"disambiguationData":[OSD([subQ0])]})])],"derivedFrom":makeQuery(id+"F14.opPattern","COPY",EDGE,{"derivedFrom":makeQuery(id+"F10.opExtrude","CAP_EDGE",EDGE,{"disambiguationData":[OSD([subQ8,subQ7,subQ6])],"isStart":false}),"instanceName":"1"})});}
            var Q16;
            {var subQ0=sQuery(id+"F0.wireOp",EDGE,"E0");var subQ6=sQuery(id+"F9.wireOp",EDGE,"E25.bottom");var subQ7=sQuery(id+"F9.wireOp",EDGE,"E24.bottom");var subQ8=sQuery(id+"F9.wireOp",EDGE,"E22.bottom");Q16=makeQuery(id+"F15.opBoolean","COPY",EDGE,{"disambiguationData":[TD([makeQuery(id+"F3.opPattern","COPY",FACE,{"derivedFrom":makeQuery(id+"F1.opExtrude","SWEPT_FACE",FACE,{"disambiguationData":[OSD([subQ0])]}),"instanceName":"1"})])],"derivedFrom":makeQuery(id+"F10.opExtrude","CAP_EDGE",EDGE,{"disambiguationData":[OSD([subQ8,subQ7,subQ6])],"isStart":false})});}
            var Q17;
            {var subQ0=sQuery(id+"F0.wireOp",EDGE,"E0");var subQ6=sQuery(id+"F9.wireOp",EDGE,"E25.bottom");var subQ7=sQuery(id+"F9.wireOp",EDGE,"E24.bottom");var subQ8=sQuery(id+"F9.wireOp",EDGE,"E22.bottom");Q17=makeQuery(id+"F15.opBoolean","COPY",EDGE,{"disambiguationData":[TD([makeQuery(id+"F3.opPattern","COPY",FACE,{"derivedFrom":makeQuery(id+"F1.opExtrude","SWEPT_FACE",FACE,{"disambiguationData":[OSD([subQ0])]}),"instanceName":"1"})])],"derivedFrom":makeQuery(id+"F10.opExtrude","CAP_EDGE",EDGE,{"disambiguationData":[OSD([subQ8,subQ7,subQ6])],"isStart":true})});}
            var Q18;
            {var subQ0=sQuery(id+"F0.wireOp",EDGE,"E0");var subQ1=sQuery(id+"F9.wireOp",EDGE,"E25.bottom");var subQ2=sQuery(id+"F9.wireOp",EDGE,"E24.bottom");var subQ3=sQuery(id+"F9.wireOp",EDGE,"E22.bottom");Q18=makeQuery(id+"F15.opBoolean","COPY",EDGE,{"disambiguationData":[TD([makeQuery(id+"F3.opPattern","COPY",FACE,{"derivedFrom":makeQuery(id+"F1.opExtrude","SWEPT_FACE",FACE,{"disambiguationData":[OSD([subQ0])]}),"instanceName":"1"})])],"derivedFrom":makeQuery(id+"F14.opPattern","COPY",EDGE,{"derivedFrom":makeQuery(id+"F10.opExtrude","CAP_EDGE",EDGE,{"disambiguationData":[OSD([subQ3,subQ2,subQ1])],"isStart":true}),"instanceName":"1"})});}
            var Q19;
            {var subQ0=sQuery(id+"F0.wireOp",EDGE,"E0");var subQ6=sQuery(id+"F9.wireOp",EDGE,"E25.bottom");var subQ7=sQuery(id+"F9.wireOp",EDGE,"E24.bottom");var subQ8=sQuery(id+"F9.wireOp",EDGE,"E22.bottom");Q19=makeQuery(id+"F15.opBoolean","COPY",EDGE,{"disambiguationData":[TD([makeQuery(id+"F3.opPattern","COPY",FACE,{"derivedFrom":makeQuery(id+"F1.opExtrude","SWEPT_FACE",FACE,{"disambiguationData":[OSD([subQ0])]}),"instanceName":"1"})])],"derivedFrom":makeQuery(id+"F14.opPattern","COPY",EDGE,{"derivedFrom":makeQuery(id+"F10.opExtrude","CAP_EDGE",EDGE,{"disambiguationData":[OSD([subQ8,subQ7,subQ6])],"isStart":false}),"instanceName":"1"})});}
            fillet(context, id + "F16", {"entities" : qUnion([Q0, Q1, Q2, Q3, Q4, Q5, Q6, Q7, Q8, Q9, Q10, Q11, Q12, Q13, Q14, Q15, Q16, Q17, Q18, Q19]), "radius" : .5 * mm, "tangentPropagation" : true, "allowEdgeOverflow" : false});
        }
    });
